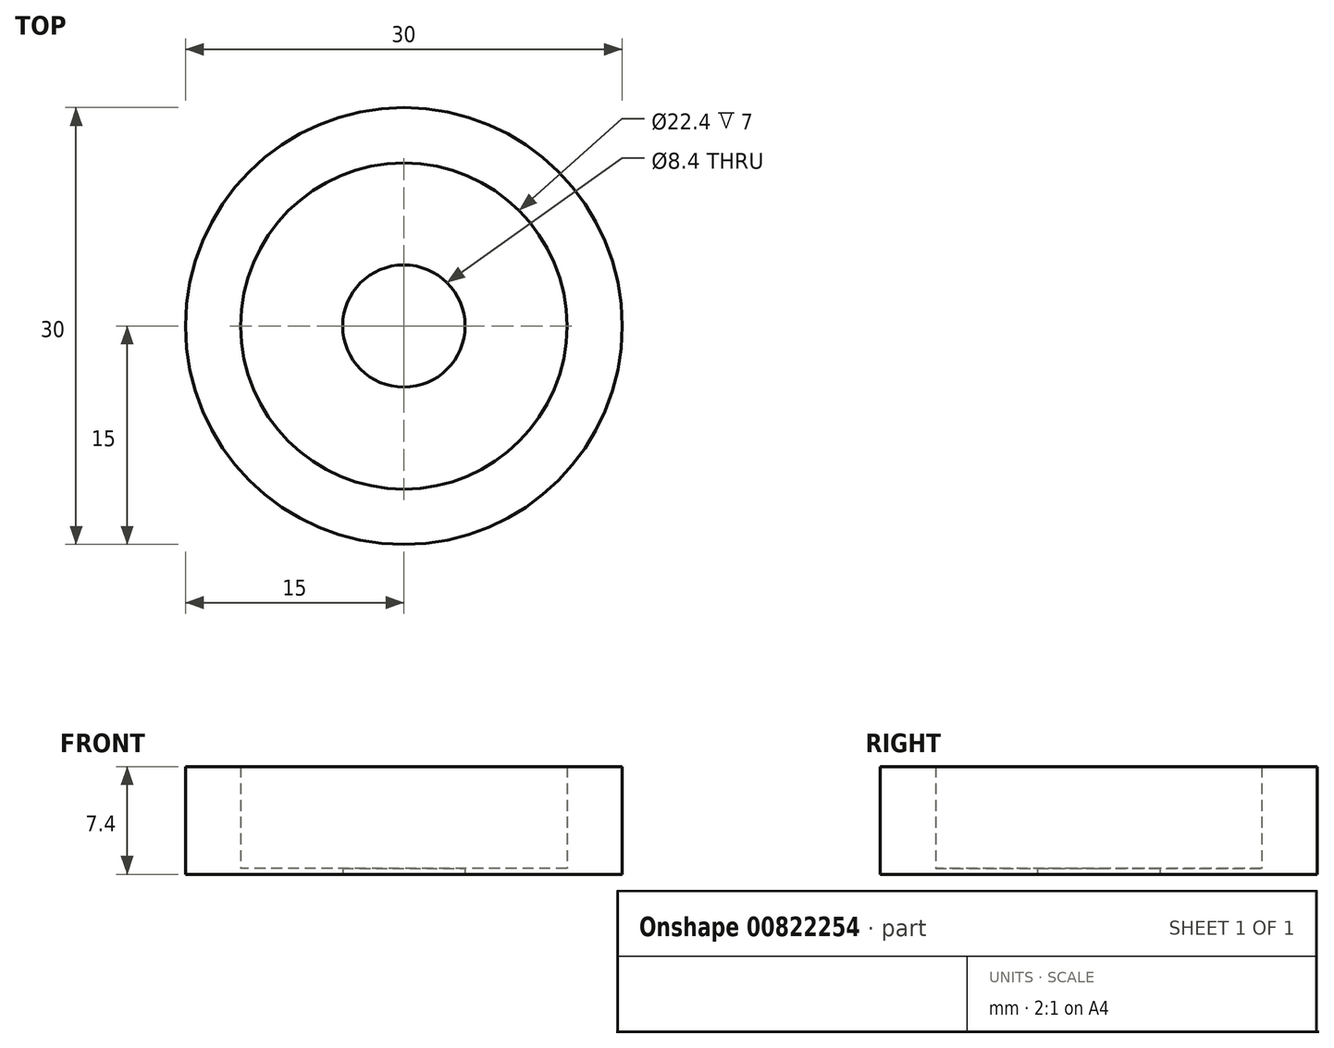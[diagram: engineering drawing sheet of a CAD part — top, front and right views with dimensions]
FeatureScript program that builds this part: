
annotation { "Feature Type Name" : "Feature", "Feature Type Description" : "" }
export const myFeature = defineFeature(function(context is Context, id is Id, definition is map)
    precondition{}
    {
        {
            var Q0;
            Q0=qCreatedBy(makeId("Top.planeOp"),FACE);
            var sketch = newSketch(context, id + "F0", { "sketchPlane" : qUnion([Q0])});
            skCircle(sketch, "E0", {"center": v(0, 0) * mm, "radius": 11.2 * mm});
            skCircle(sketch, "E1", {"center": v(0, 0) * mm, "radius": 15 * mm});
            skSolve(sketch);
        }
        {
            var Q0;
            Q0 = qSketchRegion(id + "F0", true);
            extrude(context, id + "F1", {"entities" : qUnion([Q0]), "endBound" : BoundingType.SYMMETRIC, "depth" : 7 * mm, "offsetDistance" : 25 * mm});
        }
        {
            var Q0;
            Q0=makeQuery(id+"F1.opExtrude","CAP_FACE",FACE,{"disambiguationData":[OSD([sQuery(id+"F0.wireOp",EDGE,"E0"),sQuery(id+"F0.wireOp",EDGE,"E1")])],"isStart":true});
            var sketch = newSketch(context, id + "F2", { "sketchPlane" : qUnion([Q0])});
            skCircle(sketch, "E2.0", {"center": v(0, 0) * mm, "radius": 15 * mm});
            skSolve(sketch);
        }
        {
            var Q0;
            Q0 = qSketchRegion(id + "F2", true);
            extrude(context, id + "F3", {"entities" : qUnion([Q0]), "operationType" : NewBodyOperationType.ADD, "depth" : 0.4 * mm, "offsetDistance" : 25 * mm});
        }
        {
            var Q0;
            Q0=makeQuery(id+"F3.opExtrude","CAP_FACE",FACE,{"disambiguationData":[OSD([sQuery(id+"F2.wireOp",EDGE,"E2.0")])],"isStart":false});
            var sketch = newSketch(context, id + "F4", { "sketchPlane" : qUnion([Q0])});
            skCircle(sketch, "E3", {"center": v(0, 0) * mm, "radius": 4.2 * mm});
            skSolve(sketch);
        }
        {
            var Q0;
            Q0 = qSketchRegion(id + "F4", true);
            extrude(context, id + "F5", {"entities" : qUnion([Q0]), "operationType" : NewBodyOperationType.REMOVE, "endBound" : BoundingType.THROUGH_ALL, "oppositeDirection" : true, "depth" : 25 * mm, "offsetDistance" : 25 * mm});
        }
    });
